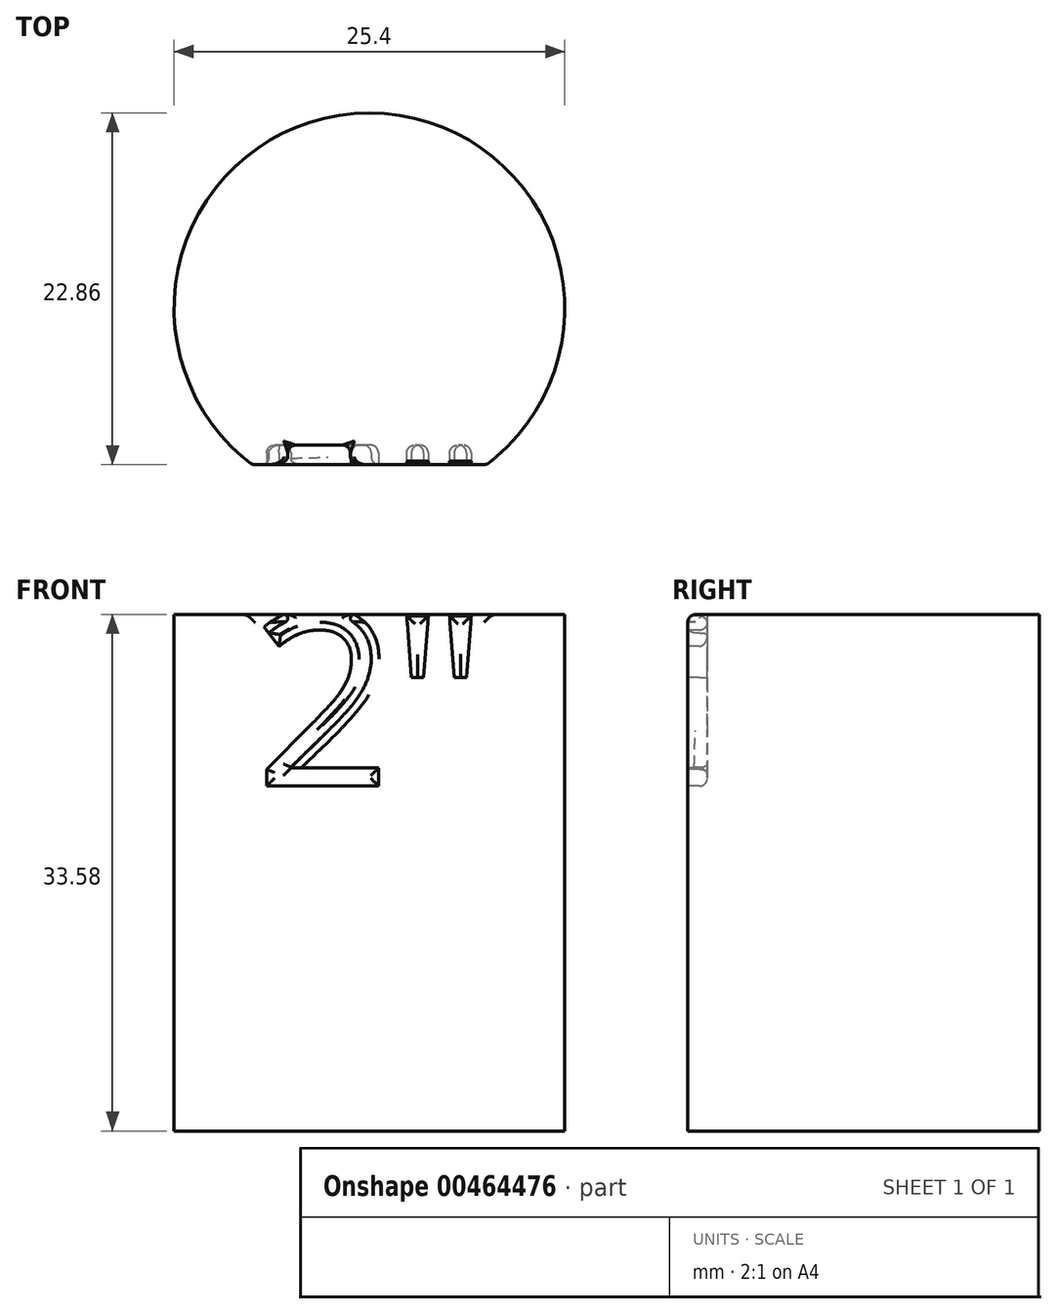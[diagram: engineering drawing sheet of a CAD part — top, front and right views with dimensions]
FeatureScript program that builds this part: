
annotation { "Feature Type Name" : "Feature", "Feature Type Description" : "" }
export const myFeature = defineFeature(function(context is Context, id is Id, definition is map)
    precondition{}
    {
        {
            var Q0;
            Q0=qCreatedBy(makeId("Top.planeOp"),FACE);
            var sketch = newSketch(context, id + "F0", { "sketchPlane" : qUnion([Q0])});
            skCircle(sketch, "E0", {"center": v(0, 0) * mm, "radius": 12.7 * mm});
            skSolve(sketch);
        }
        {
            var Q0;
            Q0 = qSketchRegion(id + "F0", true);
            extrude(context, id + "F1", {"entities" : qUnion([Q0]), "depth" : 33.58 * mm});
        }
        {
            var Q0;
            Q0=qCreatedBy(makeId("Front.planeOp"),FACE);
            cPlane(context, id + "F2", {"entities" : qUnion([Q0]), "cplaneType" : CPlaneType.OFFSET, "offset" : 12.7 * mm, "width" : 152.4 * mm, "height" : 152.4 * mm});
        }
        {
            var Q0;
            Q0=qCreatedBy(id+"F2.planeOp",FACE);
            var sketch = newSketch(context, id + "F3", { "sketchPlane" : qUnion([Q0])});
            skLineSegment(sketch, "E1.bottom", {"start": v(31.66, 44.73) * mm, "end": v(-31.66, 44.73) * mm});
            skLineSegment(sketch, "E1.top", {"start": v(31.66, -7.85) * mm, "end": v(-31.66, -7.85) * mm});
            skLineSegment(sketch, "E1.left", {"start": v(31.66, 44.73) * mm, "end": v(31.66, -7.85) * mm});
            skLineSegment(sketch, "E1.right", {"start": v(-31.66, 44.73) * mm, "end": v(-31.66, -7.85) * mm});
            skPoint(sketch, "E1.middle", {"position": v(0, 18.44) * mm});
            skSolve(sketch);
        }
        {
            var Q0;
            Q0 = qSketchRegion(id + "F3", true);
            extrude(context, id + "F4", {"entities" : qUnion([Q0]), "operationType" : NewBodyOperationType.REMOVE, "oppositeDirection" : true, "depth" : 2.54 * mm});
        }
        {
            var Q0;
            Q0=makeQuery(id+"F4.boolean.opBoolean","COPY",FACE,{"derivedFrom":makeQuery(id+"F4.opExtrude","CAP_FACE",FACE,{"disambiguationData":[OSD([sQuery(id+"F3.wireOp",EDGE,"E1.bottom"),sQuery(id+"F3.wireOp",EDGE,"E1.top"),sQuery(id+"F3.wireOp",EDGE,"E1.left"),sQuery(id+"F3.wireOp",EDGE,"E1.right")])],"isStart":false})});
            var sketch = newSketch(context, id + "F5", { "sketchPlane" : qUnion([Q0])});
            skText(sketch, "E2", { "text": "2\"", "fontName": "OpenSans-Regular.ttf"});
            const initialGuessF5  = {"E2": [-0.00744, 0.02243, 1, 0, 0.01115]};
            skSetInitialGuess(sketch, initialGuessF5);
            skSolve(sketch);
        }
        {
            var Q0;
            Q0 = qSketchRegion(id + "F5", true);
            extrude(context, id + "F6", {"entities" : qUnion([Q0]), "operationType" : NewBodyOperationType.REMOVE, "oppositeDirection" : true, "depth" : 1.27 * mm});
        }
        {
            var Q0;
            Q0=makeQuery(id+"F6.boolean.opBoolean","INTERSECT",EDGE,{"derivedFrom":[makeQuery(id+"F1.opExtrude","CAP_FACE",FACE,{"disambiguationData":[OSD([sQuery(id+"F0.wireOp",EDGE,"E0")])],"isStart":false}),makeQuery(id+"F6.opExtrude","SWEPT_FACE",FACE,{"disambiguationData":[OSD([sQuery(id+"F5.wireOp",EDGE,"E2.sketch_text.stroke-11")])]})]});
            var Q1;
            Q1=makeQuery(id+"F6.boolean.opBoolean","INTERSECT",EDGE,{"derivedFrom":[makeQuery(id+"F1.opExtrude","CAP_FACE",FACE,{"disambiguationData":[OSD([sQuery(id+"F0.wireOp",EDGE,"E0")])],"isStart":false}),makeQuery(id+"F6.opExtrude","SWEPT_FACE",FACE,{"disambiguationData":[OSD([sQuery(id+"F5.wireOp",EDGE,"E2.sketch_text.stroke-12")])]})]});
            var Q2;
            Q2=makeQuery(id+"F6.boolean.opBoolean","INTERSECT",EDGE,{"derivedFrom":[makeQuery(id+"F1.opExtrude","CAP_FACE",FACE,{"disambiguationData":[OSD([sQuery(id+"F0.wireOp",EDGE,"E0")])],"isStart":false}),makeQuery(id+"F6.opExtrude","CAP_FACE",FACE,{"disambiguationData":[OSD([sQuery(id+"F5.wireOp",EDGE,"E2.sketch_text.stroke-0"),sQuery(id+"F5.wireOp",EDGE,"E2.sketch_text.stroke-1"),sQuery(id+"F5.wireOp",EDGE,"E2.sketch_text.stroke-2"),sQuery(id+"F5.wireOp",EDGE,"E2.sketch_text.stroke-3"),sQuery(id+"F5.wireOp",EDGE,"E2.sketch_text.stroke-4"),sQuery(id+"F5.wireOp",EDGE,"E2.sketch_text.stroke-5"),sQuery(id+"F5.wireOp",EDGE,"E2.sketch_text.stroke-6"),sQuery(id+"F5.wireOp",EDGE,"E2.sketch_text.stroke-7"),sQuery(id+"F5.wireOp",EDGE,"E2.sketch_text.stroke-8"),sQuery(id+"F5.wireOp",EDGE,"E2.sketch_text.stroke-9"),sQuery(id+"F5.wireOp",EDGE,"E2.sketch_text.stroke-10"),sQuery(id+"F5.wireOp",EDGE,"E2.sketch_text.stroke-11"),sQuery(id+"F5.wireOp",EDGE,"E2.sketch_text.stroke-12"),sQuery(id+"F5.wireOp",EDGE,"E2.sketch_text.stroke-13"),sQuery(id+"F5.wireOp",EDGE,"E2.sketch_text.stroke-14"),sQuery(id+"F5.wireOp",EDGE,"E2.sketch_text.stroke-15"),sQuery(id+"F5.wireOp",EDGE,"E2.sketch_text.stroke-16"),sQuery(id+"F5.wireOp",EDGE,"E2.sketch_text.stroke-17"),sQuery(id+"F5.wireOp",EDGE,"E2.sketch_text.stroke-18"),sQuery(id+"F5.wireOp",EDGE,"E2.sketch_text.stroke-19")])],"isStart":false})]});
            fillet(context, id + "F7", {"entities" : qUnion([Q0, Q1, Q2]), "radius" : 0.25 * mm, "tangentPropagation" : true, "allowEdgeOverflow" : false});
        }
        {
            var Q0;
            Q0=makeQuery(id+"F6.boolean.opBoolean","COPY",FACE,{"derivedFrom":makeQuery(id+"F6.opExtrude","CAP_FACE",FACE,{"disambiguationData":[OSD([sQuery(id+"F5.wireOp",EDGE,"E2.sketch_text.stroke-0"),sQuery(id+"F5.wireOp",EDGE,"E2.sketch_text.stroke-1"),sQuery(id+"F5.wireOp",EDGE,"E2.sketch_text.stroke-2"),sQuery(id+"F5.wireOp",EDGE,"E2.sketch_text.stroke-3"),sQuery(id+"F5.wireOp",EDGE,"E2.sketch_text.stroke-4"),sQuery(id+"F5.wireOp",EDGE,"E2.sketch_text.stroke-5"),sQuery(id+"F5.wireOp",EDGE,"E2.sketch_text.stroke-6"),sQuery(id+"F5.wireOp",EDGE,"E2.sketch_text.stroke-7"),sQuery(id+"F5.wireOp",EDGE,"E2.sketch_text.stroke-8"),sQuery(id+"F5.wireOp",EDGE,"E2.sketch_text.stroke-9"),sQuery(id+"F5.wireOp",EDGE,"E2.sketch_text.stroke-10"),sQuery(id+"F5.wireOp",EDGE,"E2.sketch_text.stroke-11"),sQuery(id+"F5.wireOp",EDGE,"E2.sketch_text.stroke-12"),sQuery(id+"F5.wireOp",EDGE,"E2.sketch_text.stroke-13"),sQuery(id+"F5.wireOp",EDGE,"E2.sketch_text.stroke-14"),sQuery(id+"F5.wireOp",EDGE,"E2.sketch_text.stroke-15"),sQuery(id+"F5.wireOp",EDGE,"E2.sketch_text.stroke-16"),sQuery(id+"F5.wireOp",EDGE,"E2.sketch_text.stroke-17"),sQuery(id+"F5.wireOp",EDGE,"E2.sketch_text.stroke-18"),sQuery(id+"F5.wireOp",EDGE,"E2.sketch_text.stroke-19")])],"isStart":false})});
            var Q1;
            Q1=makeQuery(id+"F6.boolean.opBoolean","COPY",FACE,{"derivedFrom":makeQuery(id+"F6.opExtrude","CAP_FACE",FACE,{"disambiguationData":[OSD([sQuery(id+"F5.wireOp",EDGE,"E2.sketch_text.stroke-20"),sQuery(id+"F5.wireOp",EDGE,"E2.sketch_text.stroke-21"),sQuery(id+"F5.wireOp",EDGE,"E2.sketch_text.stroke-22"),sQuery(id+"F5.wireOp",EDGE,"E2.sketch_text.stroke-23")])],"isStart":false})});
            var Q2;
            Q2=makeQuery(id+"F6.boolean.opBoolean","COPY",FACE,{"derivedFrom":makeQuery(id+"F6.opExtrude","CAP_FACE",FACE,{"disambiguationData":[OSD([sQuery(id+"F5.wireOp",EDGE,"E2.sketch_text.stroke-24"),sQuery(id+"F5.wireOp",EDGE,"E2.sketch_text.stroke-25"),sQuery(id+"F5.wireOp",EDGE,"E2.sketch_text.stroke-26"),sQuery(id+"F5.wireOp",EDGE,"E2.sketch_text.stroke-27")])],"isStart":false})});
            var Q3;
            Q3=makeQuery(id+"F4.boolean.opBoolean","INTERSECT",EDGE,{"disambiguationData":[OD(0.0)],"derivedFrom":[makeQuery(id+"F1.opExtrude","SWEPT_FACE",FACE,{"disambiguationData":[OSD([sQuery(id+"F0.wireOp",EDGE,"E0")])]}),makeQuery(id+"F4.opExtrude","CAP_FACE",FACE,{"disambiguationData":[OSD([sQuery(id+"F3.wireOp",EDGE,"E1.bottom"),sQuery(id+"F3.wireOp",EDGE,"E1.top"),sQuery(id+"F3.wireOp",EDGE,"E1.left"),sQuery(id+"F3.wireOp",EDGE,"E1.right")])],"isStart":false})]});
            var Q4;
            Q4=makeQuery(id+"F4.boolean.opBoolean","INTERSECT",EDGE,{"disambiguationData":[OD(1.0)],"derivedFrom":[makeQuery(id+"F1.opExtrude","SWEPT_FACE",FACE,{"disambiguationData":[OSD([sQuery(id+"F0.wireOp",EDGE,"E0")])]}),makeQuery(id+"F4.opExtrude","CAP_FACE",FACE,{"disambiguationData":[OSD([sQuery(id+"F3.wireOp",EDGE,"E1.bottom"),sQuery(id+"F3.wireOp",EDGE,"E1.top"),sQuery(id+"F3.wireOp",EDGE,"E1.left"),sQuery(id+"F3.wireOp",EDGE,"E1.right")])],"isStart":false})]});
            var Q5;
            {var subQ0=sQuery(id+"F0.wireOp",EDGE,"E0");var subQ1=makeQuery(id+"F4.opExtrude","CAP_FACE",FACE,{"disambiguationData":[OSD([sQuery(id+"F3.wireOp",EDGE,"E1.bottom"),sQuery(id+"F3.wireOp",EDGE,"E1.top"),sQuery(id+"F3.wireOp",EDGE,"E1.left"),sQuery(id+"F3.wireOp",EDGE,"E1.right")])],"isStart":false});var subQ2=makeQuery(id+"F1.opExtrude","CAP_FACE",FACE,{"disambiguationData":[OSD([subQ0])],"isStart":false});Q5=makeQuery(id+"F6.boolean.opBoolean","SPLIT",EDGE,{"disambiguationData":[TD([makeQuery(id+"F6.opExtrude","SWEPT_FACE",FACE,{"disambiguationData":[OSD([sQuery(id+"F5.wireOp",EDGE,"E2.sketch_text.stroke-11")])]})])],"derivedFrom":makeQuery(id+"F4.boolean.opBoolean","INTERSECT",EDGE,{"derivedFrom":[subQ2,subQ1]})});}
            var Q6;
            {var subQ0=sQuery(id+"F0.wireOp",EDGE,"E0");var subQ1=makeQuery(id+"F4.opExtrude","CAP_FACE",FACE,{"disambiguationData":[OSD([sQuery(id+"F3.wireOp",EDGE,"E1.bottom"),sQuery(id+"F3.wireOp",EDGE,"E1.top"),sQuery(id+"F3.wireOp",EDGE,"E1.left"),sQuery(id+"F3.wireOp",EDGE,"E1.right")])],"isStart":false});var subQ2=makeQuery(id+"F1.opExtrude","CAP_FACE",FACE,{"disambiguationData":[OSD([subQ0])],"isStart":false});Q6=makeQuery(id+"F6.boolean.opBoolean","SPLIT",EDGE,{"disambiguationData":[TD([makeQuery(id+"F6.opExtrude","SWEPT_FACE",FACE,{"disambiguationData":[OSD([sQuery(id+"F5.wireOp",EDGE,"E2.sketch_text.stroke-12")])]})])],"derivedFrom":makeQuery(id+"F4.boolean.opBoolean","INTERSECT",EDGE,{"derivedFrom":[subQ2,subQ1]})});}
            var Q7;
            Q7=makeQuery(id+"F6.boolean.opBoolean","COPY",EDGE,{"derivedFrom":makeQuery(id+"F6.opExtrude","CAP_EDGE",EDGE,{"disambiguationData":[OSD([sQuery(id+"F5.wireOp",EDGE,"E2.sketch_text.stroke-18")])],"isStart":true})});
            var Q8;
            Q8=makeQuery(id+"F6.boolean.opBoolean","COPY",EDGE,{"derivedFrom":makeQuery(id+"F6.opExtrude","CAP_EDGE",EDGE,{"disambiguationData":[OSD([sQuery(id+"F5.wireOp",EDGE,"E2.sketch_text.stroke-0")])],"isStart":true})});
            var Q9;
            Q9=makeQuery(id+"F6.boolean.opBoolean","COPY",EDGE,{"derivedFrom":makeQuery(id+"F6.opExtrude","CAP_EDGE",EDGE,{"disambiguationData":[OSD([sQuery(id+"F5.wireOp",EDGE,"E2.sketch_text.stroke-19")])],"isStart":true})});
            var Q10;
            Q10=makeQuery(id+"F6.boolean.opBoolean","COPY",EDGE,{"derivedFrom":makeQuery(id+"F6.opExtrude","CAP_EDGE",EDGE,{"disambiguationData":[OSD([sQuery(id+"F5.wireOp",EDGE,"E2.sketch_text.stroke-2")])],"isStart":true})});
            var Q11;
            Q11=makeQuery(id+"F6.boolean.opBoolean","COPY",EDGE,{"derivedFrom":makeQuery(id+"F6.opExtrude","CAP_EDGE",EDGE,{"disambiguationData":[OSD([sQuery(id+"F5.wireOp",EDGE,"E2.sketch_text.stroke-5")])],"isStart":true})});
            var Q12;
            Q12=makeQuery(id+"F6.boolean.opBoolean","COPY",EDGE,{"derivedFrom":makeQuery(id+"F6.opExtrude","CAP_EDGE",EDGE,{"disambiguationData":[OSD([sQuery(id+"F5.wireOp",EDGE,"E2.sketch_text.stroke-10")])],"isStart":true})});
            var Q13;
            Q13=makeQuery(id+"F6.boolean.opBoolean","COPY",EDGE,{"derivedFrom":makeQuery(id+"F6.opExtrude","CAP_EDGE",EDGE,{"disambiguationData":[OSD([sQuery(id+"F5.wireOp",EDGE,"E2.sketch_text.stroke-1")])],"isStart":true})});
            var Q14;
            Q14=makeQuery(id+"F6.boolean.opBoolean","COPY",EDGE,{"derivedFrom":makeQuery(id+"F6.opExtrude","CAP_EDGE",EDGE,{"disambiguationData":[OSD([sQuery(id+"F5.wireOp",EDGE,"E2.sketch_text.stroke-22")])],"isStart":true})});
            var Q15;
            Q15=makeQuery(id+"F6.boolean.opBoolean","COPY",EDGE,{"derivedFrom":makeQuery(id+"F6.opExtrude","CAP_EDGE",EDGE,{"disambiguationData":[OSD([sQuery(id+"F5.wireOp",EDGE,"E2.sketch_text.stroke-21")])],"isStart":true})});
            var Q16;
            Q16=makeQuery(id+"F6.boolean.opBoolean","COPY",EDGE,{"derivedFrom":makeQuery(id+"F6.opExtrude","CAP_EDGE",EDGE,{"disambiguationData":[OSD([sQuery(id+"F5.wireOp",EDGE,"E2.sketch_text.stroke-20")])],"isStart":true})});
            var Q17;
            Q17=makeQuery(id+"F6.boolean.opBoolean","COPY",EDGE,{"derivedFrom":makeQuery(id+"F6.opExtrude","CAP_EDGE",EDGE,{"disambiguationData":[OSD([sQuery(id+"F5.wireOp",EDGE,"E2.sketch_text.stroke-23")])],"isStart":true})});
            var Q18;
            Q18=makeQuery(id+"F6.boolean.opBoolean","COPY",EDGE,{"derivedFrom":makeQuery(id+"F6.opExtrude","CAP_EDGE",EDGE,{"disambiguationData":[OSD([sQuery(id+"F5.wireOp",EDGE,"E2.sketch_text.stroke-27")])],"isStart":true})});
            var Q19;
            Q19=makeQuery(id+"F6.boolean.opBoolean","COPY",EDGE,{"derivedFrom":makeQuery(id+"F6.opExtrude","CAP_EDGE",EDGE,{"disambiguationData":[OSD([sQuery(id+"F5.wireOp",EDGE,"E2.sketch_text.stroke-26")])],"isStart":true})});
            var Q20;
            Q20=makeQuery(id+"F6.boolean.opBoolean","COPY",EDGE,{"derivedFrom":makeQuery(id+"F6.opExtrude","CAP_EDGE",EDGE,{"disambiguationData":[OSD([sQuery(id+"F5.wireOp",EDGE,"E2.sketch_text.stroke-25")])],"isStart":true})});
            var Q21;
            Q21=makeQuery(id+"F6.boolean.opBoolean","COPY",EDGE,{"derivedFrom":makeQuery(id+"F6.opExtrude","CAP_EDGE",EDGE,{"disambiguationData":[OSD([sQuery(id+"F5.wireOp",EDGE,"E2.sketch_text.stroke-24")])],"isStart":true})});
            fillet(context, id + "F8", {"entities" : qUnion([Q0, Q1, Q2, Q3, Q4, Q5, Q6, Q7, Q8, Q9, Q10, Q11, Q12, Q13, Q14, Q15, Q16, Q17, Q18, Q19, Q20, Q21]), "radius" : 0.5 * mm, "tangentPropagation" : true, "allowEdgeOverflow" : false});
        }
    });
